# Revit family: P500321-009-30
name_source: partatom
category: Lighting Fixtures
revit_build: Autodesk Revit 2014 (Build: 20130308_1515(x64)
units: mm (PartAtom-declared; Revit-internal decimal feet)

## types (1)
- P500321-009-30
    Apparent Load = 7 VA
    Assembly Code = D5020200
    Color Filter = 16777215
    Connector Description = Lighting Connector
    Default Elevation = 48 "
    Description = Manifest a futuristic effect with the Kylo LED Collection 1-Light Brushed Nickel Frosted Acrylic LED Modern Hanging Pendant Light. Sleek metal light base coated in a beautiful brushed nickel finish and attached to a steel cable is sure to add drama to a room's design. Crisp frosted shade creates a seamless tube of illumination.
    Dimming Lamp Color Temperature Shift = <None>
    Features = Application: Manifest a futuristic effect with the Kylo LED Collection 1-Light Brushed Nickel Frosted Acrylic LED Modern Hanging Pendant Light ideal for any foyer, dining room, kitchen, breakfast nook, entryway, living room, or stairway.
Styles: Perfect for modern, contemporary, and mid-century modern style settings.
Finish: Sleek metal light base coated in a beautiful brushed nickel finish and attached to a steel cable is sure to add drama to a room's design.
Materials: Constructed from aluminum to ensure a long product lifespan.
Glass/Shades: Crisp frosted shade creates a seamless tube of illumination.
Bulbs: For ideal illumination, 1 integrated LED modules are included (6.5w)
3000K
90CRI
420 delivered lumens.
Dimensions: Measures 4-3/4-inch diameter by 13-inch height.
Certifications: cETLus damp location listed, meets California Title 24 JA8-2019.
Pairs With: Pairs with a variety of lighting fixtures.
Warranty: Our 5-Limited Warranty guarantees your complete satisfaction with your purchase and includes professional after-sales customer service support.
    Fixture distribution = Direct
    Glass = Paint - Hubbell - White Texture
    Gold = Hubbell Metal Brass
    Housing Material = Paint - Hubbell - Textured Camera Black
    Lamp = LED
    Load Classification = Lighting
    Manufacturer = Progress Lighting
    Model = P500321-009-30
    Photometric Web File = generic.ies
    Power Factor = 1
    Product Link = https://www.hubbell.com
    Support = Paint - Hubbell - Light Silver
    Tilt Angle = -90.00°
    URL = https://www.hubbell.com
    Voltage = 120 V
    Warranty = 5 year Warranty
    Wattage Comments = 60W
    Watts = 7 W

## geometry (parser evidence)
native form markers: Sweep x4
no freeform markers — native parametric forms only
